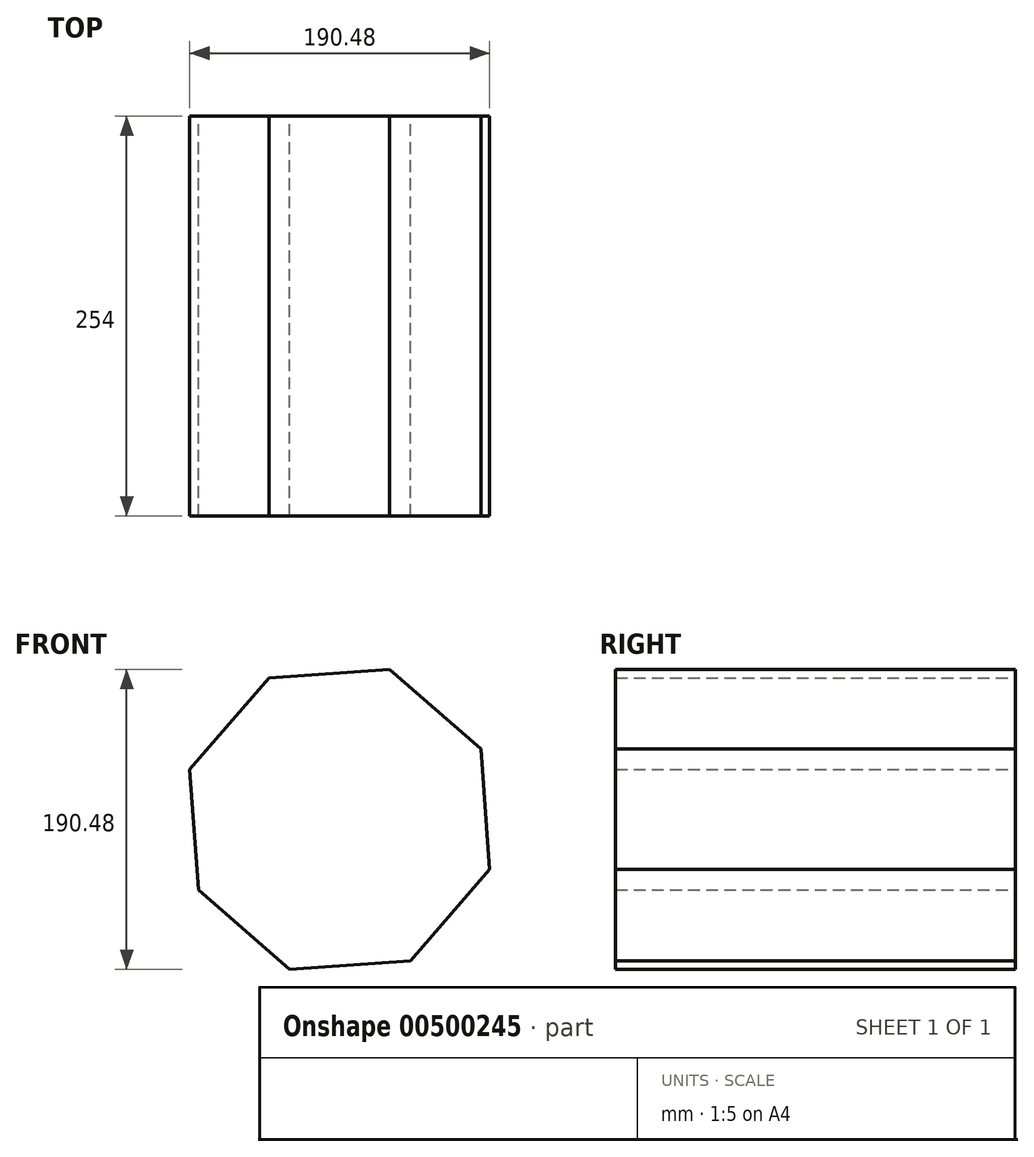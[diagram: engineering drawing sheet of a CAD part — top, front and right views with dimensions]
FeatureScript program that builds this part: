
annotation { "Feature Type Name" : "Feature", "Feature Type Description" : "" }
export const myFeature = defineFeature(function(context is Context, id is Id, definition is map)
    precondition{}
    {
        {
            var Q0;
            Q0=qCreatedBy(makeId("Front.planeOp"),FACE);
            var sketch = newSketch(context, id + "F0", { "sketchPlane" : qUnion([Q0])});
            skCircle(sketch, "E0.cCircle", {"center": v(0, 0) * mm, "radius": 100.4 * mm, "construction": true});
            skLineSegment(sketch, "E0.0", {"start": v(-89.8, -44.9) * mm, "end": v(-95.24, 31.75) * mm});
            skLineSegment(sketch, "E0.1", {"start": v(-95.24, 31.75) * mm, "end": v(-44.9, 89.8) * mm});
            skLineSegment(sketch, "E0.2", {"start": v(-44.9, 89.8) * mm, "end": v(31.75, 95.24) * mm});
            skLineSegment(sketch, "E0.3", {"start": v(31.75, 95.24) * mm, "end": v(89.8, 44.9) * mm});
            skLineSegment(sketch, "E0.4", {"start": v(89.8, 44.9) * mm, "end": v(95.24, -31.75) * mm});
            skLineSegment(sketch, "E0.5", {"start": v(95.24, -31.75) * mm, "end": v(44.9, -89.8) * mm});
            skLineSegment(sketch, "E0.6", {"start": v(44.9, -89.8) * mm, "end": v(-31.75, -95.24) * mm});
            skLineSegment(sketch, "E0.7", {"start": v(-31.75, -95.24) * mm, "end": v(-89.8, -44.9) * mm});
            skSolve(sketch);
        }
        {
            var Q0;
            Q0=makeQuery(id+"F0.imprint","IMPRINT",FACE,{"disambiguationData":[TD([[makeQuery(id+"F0.imprint","IMPRINT",EDGE,{"derivedFrom":sQuery(id+"F0.wireOp",EDGE,"E0.0")}),-1.0]])]});
            extrude(context, id + "F1", {"entities" : qUnion([Q0]), "depth" : 254 * mm});
        }
    });
